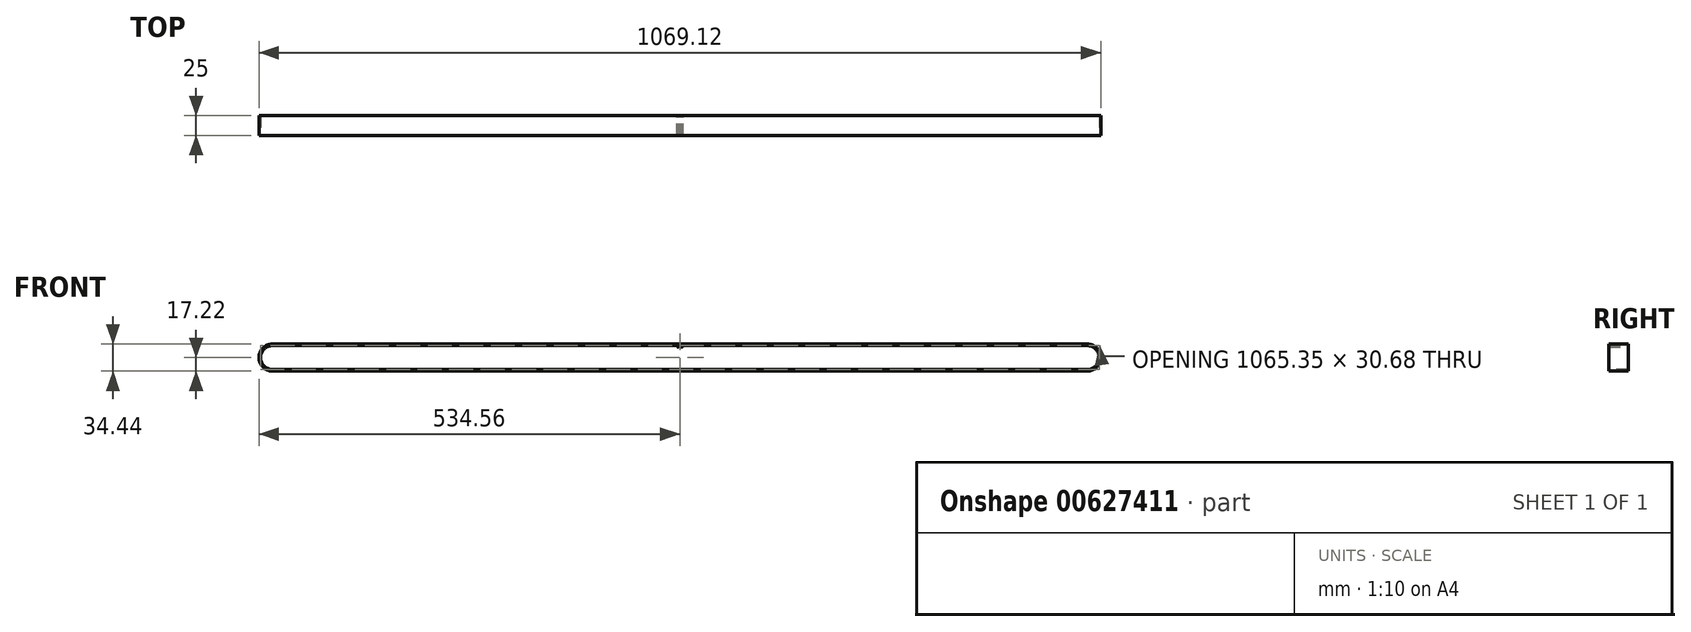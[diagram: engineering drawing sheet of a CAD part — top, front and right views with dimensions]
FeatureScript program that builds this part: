
annotation { "Feature Type Name" : "Feature", "Feature Type Description" : "" }
export const myFeature = defineFeature(function(context is Context, id is Id, definition is map)
    precondition{}
    {
        {
            var Q0;
            Q0=qCreatedBy(makeId("Front.planeOp"),FACE);
            var sketch = newSketch(context, id + "F0", { "sketchPlane" : qUnion([Q0])});
            skLineSegment(sketch, "E0", {"start": v(-517.33, 0) * mm, "end": v(517.33, 0) * mm, "construction": true});
            skArc(sketch, "E1.0.startCap", {"start": v(-517.33, -15.34) * mm, "mid": v(-532.68, 0) * mm, "end": v(-517.33, 15.34) * mm});
            skArc(sketch, "E1.0.endCap", {"start": v(517.33, 15.34) * mm, "mid": v(532.68, 0) * mm, "end": v(517.33, -15.34) * mm});
            skLineSegment(sketch, "E1.0.left", {"start": v(-517.33, 15.34) * mm, "end": v(517.33, 15.34) * mm});
            skLineSegment(sketch, "E1.0.right", {"start": v(-517.33, -15.34) * mm, "end": v(517.33, -15.34) * mm});
            skLineSegment(sketch, "E2.0", {"start": v(-517.33, 17.22) * mm, "end": v(517.33, 17.22) * mm});
            skArc(sketch, "E2.1", {"start": v(-517.33, -17.22) * mm, "mid": v(-534.56, 0) * mm, "end": v(-517.33, 17.22) * mm});
            skLineSegment(sketch, "E2.2", {"start": v(-517.33, -17.22) * mm, "end": v(517.33, -17.22) * mm});
            skArc(sketch, "E2.3", {"start": v(517.33, 17.22) * mm, "mid": v(534.56, 0) * mm, "end": v(517.33, -17.22) * mm});
            skSolve(sketch);
        }
        {
            var Q0;
            Q0 = qSketchRegion(id + "F0", true);
            extrude(context, id + "F1", {"entities" : qUnion([Q0]), "endBound" : BoundingType.SYMMETRIC, "oppositeDirection" : true, "depth" : 25 * mm, "offsetDistance" : 25.4 * mm});
        }
        {
            var Q0;
            Q0=qCreatedBy(makeId("Front.planeOp"),FACE);
            var sketch = newSketch(context, id + "F2", { "sketchPlane" : qUnion([Q0])});
            skArc(sketch, "E3.0", {"start": v(-3.97, 14.92) * mm, "mid": v(-4.15, 15.22) * mm, "end": v(-4.48, 15.34) * mm});
            skArc(sketch, "E4.0", {"start": v(-3.97, 14.92) * mm, "mid": v(-3.89, 14.57) * mm, "end": v(-3.76, 14.23) * mm});
            skArc(sketch, "E5.0", {"start": v(-3.76, 14.23) * mm, "mid": v(-2.5, 13.41) * mm, "end": v(-1.24, 14.23) * mm});
            skArc(sketch, "E6.0", {"start": v(-1.24, 14.23) * mm, "mid": v(-1.11, 14.57) * mm, "end": v(-1.03, 14.92) * mm});
            skArc(sketch, "E7.0", {"start": v(-0.52, 15.34) * mm, "mid": v(-0.85, 15.22) * mm, "end": v(-1.03, 14.92) * mm});
            skLineSegment(sketch, "E8.0", {"start": v(0.52, 15.34) * mm, "end": v(-0.52, 15.34) * mm});
            skArc(sketch, "E9.0", {"start": v(1.03, 14.92) * mm, "mid": v(0.85, 15.22) * mm, "end": v(0.52, 15.34) * mm});
            skArc(sketch, "E10.0", {"start": v(1.03, 14.92) * mm, "mid": v(1.11, 14.57) * mm, "end": v(1.24, 14.23) * mm});
            skArc(sketch, "E11.0", {"start": v(1.24, 14.23) * mm, "mid": v(2.5, 13.41) * mm, "end": v(3.76, 14.23) * mm});
            skArc(sketch, "E12.0", {"start": v(3.76, 14.23) * mm, "mid": v(3.89, 14.57) * mm, "end": v(3.97, 14.92) * mm});
            skArc(sketch, "E13.0", {"start": v(4.48, 15.34) * mm, "mid": v(4.15, 15.22) * mm, "end": v(3.97, 14.92) * mm});
            skLineSegment(sketch, "E14", {"start": v(-2.5, 14.78) * mm, "end": v(2.5, 14.78) * mm, "construction": true});
            skLineSegment(sketch, "E15", {"start": v(-3.53, 15.34) * mm, "end": v(3.53, 15.34) * mm, "construction": true});
            skLineSegment(sketch, "E16", {"start": v(-4.48, 14.83) * mm, "end": v(4.48, 14.83) * mm, "construction": true});
            skLineSegment(sketch, "E17", {"start": v(-3.97, 14.92) * mm, "end": v(3.97, 14.92) * mm, "construction": true});
            skLineSegment(sketch, "E18", {"start": v(-3.76, 14.23) * mm, "end": v(3.76, 14.23) * mm, "construction": true});
            skLineSegment(sketch, "E19", {"start": v(-4.48, 15.34) * mm, "end": v(-4.48, 15.85) * mm});
            skLineSegment(sketch, "E20", {"start": v(-4.48, 15.85) * mm, "end": v(4.48, 15.85) * mm});
            skLineSegment(sketch, "E21", {"start": v(4.48, 15.85) * mm, "end": v(4.48, 15.34) * mm});
            skSolve(sketch);
        }
        {
            var Q0;
            Q0 = qSketchRegion(id + "F2", true);
            extrude(context, id + "F3", {"entities" : qUnion([Q0]), "operationType" : NewBodyOperationType.ADD, "endBound" : BoundingType.SYMMETRIC, "depth" : 25 * mm, "offsetDistance" : 25.4 * mm});
        }
    });
